# Revit family: Door_Cladding-Construction_Specialties
name_source: partatom
category: Specialty Equipment
revit_build: Autodesk Revit 2017 (Build: 20160225_1515(x64)
units: mm (PartAtom-declared; Revit-internal decimal feet)

## family parameters
Always vertical = Yes
Cut with Voids When Loaded = No
Part Type = Normal
Room Calculation Point = No
Round Connector Dimension = Use Diameter
Shared = Yes
Work Plane-Based = No

## types (3) — shared parameters
Assembly Code = C1020
Description = Acrovyn door cladding is available in .040" (1.02mm) and .060" (1.52mm) thick Acrovyn sheets supplied in standard door width/height with a 90 degree edge.
Manufacturer = Construction Specialties
Product Documentation Link = https://www.c-sgroup.com
Product Page URL = https://www.c-sgroup.com
URL = https://www.c-sgroup.com

## per-type parameters (varying)
| type | Cladding | Cladding Thickness | Model |
| .040" | Yes | 0' - 0 1/32" | 3DPN - .040" (1.02mm) |
| None | No | 0' - 0 1/16" | NONE - Choose Cladding Type per Door |
| .060" | Yes | 0' - 0 1/16" | 3DPN - .060" (1.52mm) |

## geometry (parser evidence)
native form markers: Sweep x2
no freeform markers — native parametric forms only
